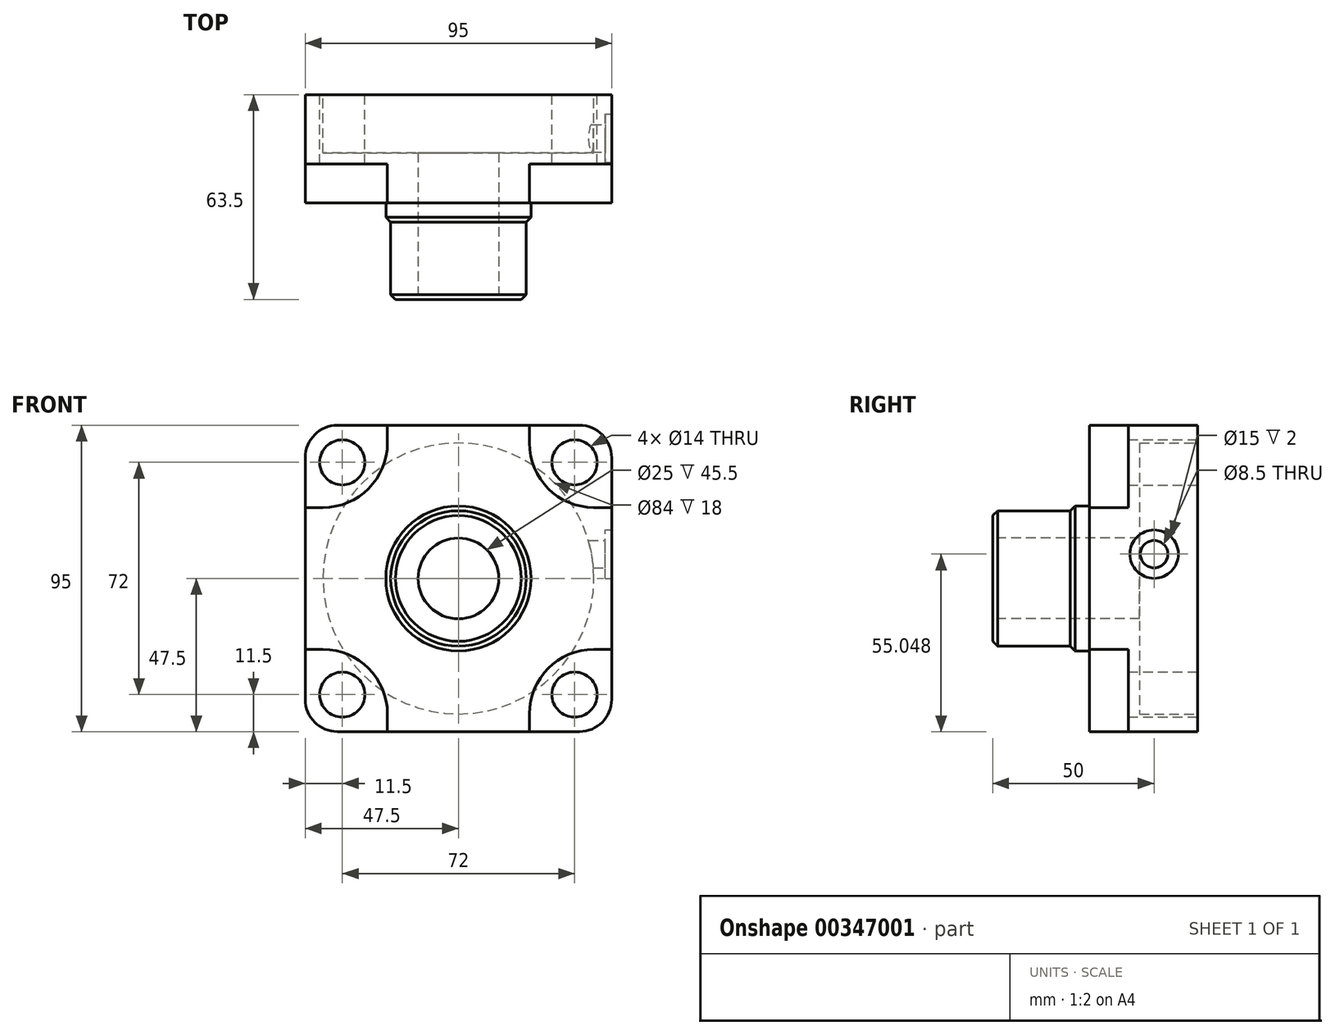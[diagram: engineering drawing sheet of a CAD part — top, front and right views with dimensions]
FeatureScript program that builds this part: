
annotation { "Feature Type Name" : "Feature", "Feature Type Description" : "" }
export const myFeature = defineFeature(function(context is Context, id is Id, definition is map)
    precondition{}
    {
        {
            var Q0;
            Q0=qCreatedBy(makeId("Front.planeOp"),FACE);
            var sketch = newSketch(context, id + "F0", { "sketchPlane" : qUnion([Q0])});
            skLineSegment(sketch, "E0.bottom", {"start": v(37.5, -47.5) * mm, "end": v(-37.5, -47.5) * mm});
            skLineSegment(sketch, "E0.top", {"start": v(37.5, 47.5) * mm, "end": v(-37.5, 47.5) * mm});
            skLineSegment(sketch, "E0.left", {"start": v(47.5, -37.5) * mm, "end": v(47.5, 37.5) * mm});
            skLineSegment(sketch, "E0.right", {"start": v(-47.5, -37.5) * mm, "end": v(-47.5, 37.5) * mm});
            skPoint(sketch, "E0.middle", {"position": v(0, 0) * mm});
            skPoint(sketch, "E1.visualSharp", {"position": v(-47.5, 47.5) * mm});
            skArc(sketch, "E1.filletArc", {"start": v(-37.5, 47.5) * mm, "mid": v(-44.57, 44.57) * mm, "end": v(-47.5, 37.5) * mm});
            skPoint(sketch, "E2.visualSharp", {"position": v(47.5, 47.5) * mm});
            skArc(sketch, "E2.filletArc", {"start": v(47.5, 37.5) * mm, "mid": v(44.57, 44.57) * mm, "end": v(37.5, 47.5) * mm});
            skPoint(sketch, "E3.visualSharp", {"position": v(47.5, -47.5) * mm});
            skArc(sketch, "E3.filletArc", {"start": v(37.5, -47.5) * mm, "mid": v(44.57, -44.57) * mm, "end": v(47.5, -37.5) * mm});
            skPoint(sketch, "E4.visualSharp", {"position": v(-47.5, -47.5) * mm});
            skArc(sketch, "E4.filletArc", {"start": v(-47.5, -37.5) * mm, "mid": v(-44.57, -44.57) * mm, "end": v(-37.5, -47.5) * mm});
            skLineSegment(sketch, "E5", {"start": v(0, 47.5) * mm, "end": v(0, -47.5) * mm, "construction": true});
            skLineSegment(sketch, "E6.0", {"start": v(-36, 47.5) * mm, "end": v(-36, -47.5) * mm, "construction": true});
            skLineSegment(sketch, "E7.0", {"start": v(36, 47.5) * mm, "end": v(36, -47.5) * mm, "construction": true});
            skLineSegment(sketch, "E8", {"start": v(-47.5, 0) * mm, "end": v(47.5, 0) * mm, "construction": true});
            skLineSegment(sketch, "E9.0", {"start": v(-47.5, -36) * mm, "end": v(47.5, -36) * mm, "construction": true});
            skLineSegment(sketch, "E10.0", {"start": v(-47.5, 36) * mm, "end": v(47.5, 36) * mm, "construction": true});
            skCircle(sketch, "E11", {"center": v(-36, 36) * mm, "radius": 7 * mm});
            skCircle(sketch, "E12", {"center": v(36, 36) * mm, "radius": 7 * mm});
            skCircle(sketch, "E13", {"center": v(-36, -36) * mm, "radius": 7 * mm});
            skCircle(sketch, "E14", {"center": v(36, -36) * mm, "radius": 7 * mm});
            skSolve(sketch);
        }
        {
            var Q0;
            Q0=makeQuery(id+"F0.imprint","IMPRINT",FACE,{"disambiguationData":[TD([[makeQuery(id+"F0.imprint","IMPRINT",EDGE,{"derivedFrom":sQuery(id+"F0.wireOp",EDGE,"E0.bottom")}),-1.0]])]});
            extrude(context, id + "F1", {"entities" : qUnion([Q0]), "endBound" : BoundingType.SYMMETRIC, "depth" : 33.5 * mm});
        }
        {
            var Q0;
            Q0=makeQuery(id+"F1.opExtrude","CAP_FACE",FACE,{"disambiguationData":[OSD([sQuery(id+"F0.wireOp",EDGE,"E0.bottom"),sQuery(id+"F0.wireOp",EDGE,"E0.top"),sQuery(id+"F0.wireOp",EDGE,"E0.left"),sQuery(id+"F0.wireOp",EDGE,"E0.right"),sQuery(id+"F0.wireOp",EDGE,"E1.filletArc"),sQuery(id+"F0.wireOp",EDGE,"E2.filletArc"),sQuery(id+"F0.wireOp",EDGE,"E3.filletArc"),sQuery(id+"F0.wireOp",EDGE,"E4.filletArc"),sQuery(id+"F0.wireOp",EDGE,"E11"),sQuery(id+"F0.wireOp",EDGE,"E12"),sQuery(id+"F0.wireOp",EDGE,"E13"),sQuery(id+"F0.wireOp",EDGE,"E14")])],"isStart":false});
            var sketch = newSketch(context, id + "F2", { "sketchPlane" : qUnion([Q0])});
            skLineSegment(sketch, "E15", {"start": v(-47.5, 22) * mm, "end": v(-42, 22) * mm});
            skLineSegment(sketch, "E16", {"start": v(-47.5, -22) * mm, "end": v(-42, -22) * mm});
            skLineSegment(sketch, "E17", {"start": v(-22, 47.5) * mm, "end": v(-22, 42) * mm});
            skLineSegment(sketch, "E18", {"start": v(22, 47.5) * mm, "end": v(22, 42) * mm});
            skLineSegment(sketch, "E19", {"start": v(42, 22) * mm, "end": v(47.5, 22) * mm});
            skLineSegment(sketch, "E20", {"start": v(42, -22) * mm, "end": v(47.5, -22) * mm});
            skLineSegment(sketch, "E21", {"start": v(22, -42) * mm, "end": v(22, -47.5) * mm});
            skLineSegment(sketch, "E22", {"start": v(-22, -42) * mm, "end": v(-22, -47.5) * mm});
            skArc(sketch, "E23.filletArc", {"start": v(-42, 22) * mm, "mid": v(-27.86, 27.86) * mm, "end": v(-22, 42) * mm});
            skPoint(sketch, "E24.newPointA", {"position": v(0.48, 22) * mm});
            skArc(sketch, "E24.filletArc", {"start": v(22, 42) * mm, "mid": v(27.86, 27.86) * mm, "end": v(42, 22) * mm});
            skPoint(sketch, "E25.newPointB", {"position": v(-22, -0.08) * mm});
            skArc(sketch, "E25.filletArc", {"start": v(-22, -42) * mm, "mid": v(-27.86, -27.86) * mm, "end": v(-42, -22) * mm});
            skPoint(sketch, "E26.newPointA", {"position": v(1.13, -22) * mm});
            skPoint(sketch, "E26.newPointB", {"position": v(22, -0.08) * mm});
            skArc(sketch, "E26.filletArc", {"start": v(42, -22) * mm, "mid": v(27.86, -27.86) * mm, "end": v(22, -42) * mm});
            skLineSegment(sketch, "E27.0", {"start": v(-47.5, -37.5) * mm, "end": v(-47.5, -22) * mm});
            skArc(sketch, "E28.0", {"start": v(-37.5, 47.5) * mm, "mid": v(-44.57, 44.57) * mm, "end": v(-47.5, 37.5) * mm});
            skLineSegment(sketch, "E29.0", {"start": v(37.5, 47.5) * mm, "end": v(22, 47.5) * mm});
            skPoint(sketch, "E30.0", {"position": v(44.57, 44.57) * mm});
            skArc(sketch, "E31.0", {"start": v(47.5, 37.5) * mm, "mid": v(44.57, 44.57) * mm, "end": v(37.5, 47.5) * mm});
            skLineSegment(sketch, "E32.0", {"start": v(47.5, -37.5) * mm, "end": v(47.5, -22) * mm});
            skPoint(sketch, "E33.0", {"position": v(44.57, -44.57) * mm});
            skArc(sketch, "E34.0", {"start": v(37.5, -47.5) * mm, "mid": v(44.57, -44.57) * mm, "end": v(47.5, -37.5) * mm});
            skLineSegment(sketch, "E35.0", {"start": v(37.5, -47.5) * mm, "end": v(22, -47.5) * mm});
            skArc(sketch, "E36.0", {"start": v(-47.5, -37.5) * mm, "mid": v(-44.57, -44.57) * mm, "end": v(-37.5, -47.5) * mm});
            skPoint(sketch, "E37.orphan", {"position": v(-51.1, 22) * mm});
            skPoint(sketch, "E38.orphan", {"position": v(-22, 52.95) * mm});
            skLineSegment(sketch, "E39.trimOffspring", {"start": v(-22, 47.5) * mm, "end": v(-37.5, 47.5) * mm});
            skLineSegment(sketch, "E40.trimOffspring", {"start": v(-47.5, 22) * mm, "end": v(-47.5, 37.5) * mm});
            skPoint(sketch, "E41.orphan", {"position": v(-22, -53.12) * mm});
            skPoint(sketch, "E42.orphan", {"position": v(-51.1, -22) * mm});
            skLineSegment(sketch, "E43.trimOffspring", {"start": v(-22, -47.5) * mm, "end": v(-37.5, -47.5) * mm});
            skPoint(sketch, "E44.orphan", {"position": v(22, -51.66) * mm});
            skPoint(sketch, "E45.orphan", {"position": v(53.36, -22) * mm});
            skPoint(sketch, "E46.orphan", {"position": v(52.07, 22) * mm});
            skPoint(sketch, "E47.orphan", {"position": v(22, 51.5) * mm});
            skLineSegment(sketch, "E48.trimOffspring", {"start": v(47.5, 22) * mm, "end": v(47.5, 37.5) * mm});
            skSolve(sketch);
        }
        {
            var Q0;
            Q0=makeQuery(id+"F2.imprint","IMPRINT",FACE,{"disambiguationData":[TD([[makeQuery(id+"F2.imprint","IMPRINT",EDGE,{"derivedFrom":sQuery(id+"F2.wireOp",EDGE,"E20")}),-1.0]])]});
            var Q1;
            Q1=makeQuery(id+"F2.imprint","IMPRINT",FACE,{"disambiguationData":[TD([[makeQuery(id+"F2.imprint","IMPRINT",EDGE,{"derivedFrom":sQuery(id+"F2.wireOp",EDGE,"E18")}),1.0]])]});
            var Q2;
            Q2=makeQuery(id+"F2.imprint","IMPRINT",FACE,{"disambiguationData":[TD([[makeQuery(id+"F2.imprint","IMPRINT",EDGE,{"derivedFrom":sQuery(id+"F2.wireOp",EDGE,"E15")}),1.0]])]});
            var Q3;
            Q3=makeQuery(id+"F2.imprint","IMPRINT",FACE,{"disambiguationData":[TD([[makeQuery(id+"F2.imprint","IMPRINT",EDGE,{"derivedFrom":sQuery(id+"F2.wireOp",EDGE,"E16")}),-1.0]])]});
            extrude(context, id + "F3", {"entities" : qUnion([Q0, Q1, Q2, Q3]), "operationType" : NewBodyOperationType.REMOVE, "oppositeDirection" : true, "depth" : 12 * mm});
        }
        {
            var Q0;
            Q0=makeQuery(id+"F1.opExtrude","CAP_FACE",FACE,{"disambiguationData":[OSD([sQuery(id+"F0.wireOp",EDGE,"E0.bottom"),sQuery(id+"F0.wireOp",EDGE,"E0.top"),sQuery(id+"F0.wireOp",EDGE,"E0.left"),sQuery(id+"F0.wireOp",EDGE,"E0.right"),sQuery(id+"F0.wireOp",EDGE,"E1.filletArc"),sQuery(id+"F0.wireOp",EDGE,"E2.filletArc"),sQuery(id+"F0.wireOp",EDGE,"E3.filletArc"),sQuery(id+"F0.wireOp",EDGE,"E4.filletArc"),sQuery(id+"F0.wireOp",EDGE,"E11"),sQuery(id+"F0.wireOp",EDGE,"E12"),sQuery(id+"F0.wireOp",EDGE,"E13"),sQuery(id+"F0.wireOp",EDGE,"E14")])],"isStart":false});
            var sketch = newSketch(context, id + "F4", { "sketchPlane" : qUnion([Q0])});
            skCircle(sketch, "E49", {"center": v(0, 0) * mm, "radius": 22.5 * mm});
            skSolve(sketch);
        }
        {
            var Q0;
            Q0=makeQuery(id+"F4.imprint","IMPRINT",FACE,{"disambiguationData":[TD([[makeQuery(id+"F4.imprint","IMPRINT",EDGE,{"derivedFrom":sQuery(id+"F4.wireOp",EDGE,"E49")}),1.0]])]});
            extrude(context, id + "F5", {"entities" : qUnion([Q0]), "operationType" : NewBodyOperationType.ADD, "depth" : 6 * mm});
        }
        {
            var Q0;
            Q0=makeQuery(id+"F5.opExtrude","CAP_EDGE",EDGE,{"disambiguationData":[OSD([sQuery(id+"F4.wireOp",EDGE,"E49")])],"isStart":false});
            chamfer(context, id + "F6", {"entities" : qUnion([Q0]), "width" : 1.5 * mm, "tangentPropagation" : true});
        }
        {
            var Q0;
            Q0=makeQuery(id+"F5.opExtrude","CAP_FACE",FACE,{"disambiguationData":[OSD([sQuery(id+"F4.wireOp",EDGE,"E49")])],"isStart":false});
            var sketch = newSketch(context, id + "F7", { "sketchPlane" : qUnion([Q0])});
            skCircle(sketch, "E50.0", {"center": v(0, 0) * mm, "radius": 21 * mm});
            skSolve(sketch);
        }
        {
            var Q0;
            Q0=makeQuery(id+"F7.imprint","IMPRINT",FACE,{"disambiguationData":[TD([[makeQuery(id+"F7.imprint","IMPRINT",EDGE,{"derivedFrom":sQuery(id+"F7.wireOp",EDGE,"E50.0")}),1.0]])]});
            extrude(context, id + "F8", {"entities" : qUnion([Q0]), "operationType" : NewBodyOperationType.ADD, "depth" : 24 * mm});
        }
        {
            var Q0;
            Q0=makeQuery(id+"F8.opExtrude","CAP_EDGE",EDGE,{"disambiguationData":[OSD([sQuery(id+"F7.wireOp",EDGE,"E50.0")])],"isStart":false});
            chamfer(context, id + "F9", {"entities" : qUnion([Q0]), "width" : 1.5 * mm, "tangentPropagation" : true});
        }
        {
            var Q0;
            Q0=makeQuery(id+"F8.opExtrude","CAP_FACE",FACE,{"disambiguationData":[OSD([sQuery(id+"F7.wireOp",EDGE,"E50.0")])],"isStart":false});
            var sketch = newSketch(context, id + "F10", { "sketchPlane" : qUnion([Q0])});
            skCircle(sketch, "E51", {"center": v(0, 0) * mm, "radius": 12.5 * mm});
            skSolve(sketch);
        }
        {
            var Q0;
            Q0=makeQuery(id+"F10.imprint","IMPRINT",FACE,{"disambiguationData":[TD([[makeQuery(id+"F10.imprint","IMPRINT",EDGE,{"derivedFrom":sQuery(id+"F10.wireOp",EDGE,"E51")}),1.0]])]});
            extrude(context, id + "F11", {"entities" : qUnion([Q0]), "operationType" : NewBodyOperationType.REMOVE, "endBound" : BoundingType.THROUGH_ALL, "oppositeDirection" : true, "depth" : 25 * mm});
        }
        {
            var Q0;
            Q0=makeQuery(id+"F1.opExtrude","CAP_FACE",FACE,{"disambiguationData":[OSD([sQuery(id+"F0.wireOp",EDGE,"E0.bottom"),sQuery(id+"F0.wireOp",EDGE,"E0.top"),sQuery(id+"F0.wireOp",EDGE,"E0.left"),sQuery(id+"F0.wireOp",EDGE,"E0.right"),sQuery(id+"F0.wireOp",EDGE,"E1.filletArc"),sQuery(id+"F0.wireOp",EDGE,"E2.filletArc"),sQuery(id+"F0.wireOp",EDGE,"E3.filletArc"),sQuery(id+"F0.wireOp",EDGE,"E4.filletArc"),sQuery(id+"F0.wireOp",EDGE,"E11"),sQuery(id+"F0.wireOp",EDGE,"E12"),sQuery(id+"F0.wireOp",EDGE,"E13"),sQuery(id+"F0.wireOp",EDGE,"E14")])],"isStart":true});
            var sketch = newSketch(context, id + "F12", { "sketchPlane" : qUnion([Q0])});
            skCircle(sketch, "E52", {"center": v(0, 0) * mm, "radius": 42 * mm});
            skSolve(sketch);
        }
        {
            var Q0;
            Q0=makeQuery(id+"F12.imprint","IMPRINT",FACE,{"disambiguationData":[TD([[makeQuery(id+"F12.imprint","IMPRINT",EDGE,{"derivedFrom":sQuery(id+"F12.wireOp",EDGE,"E52")}),1.0]])]});
            extrude(context, id + "F13", {"entities" : qUnion([Q0]), "operationType" : NewBodyOperationType.REMOVE, "oppositeDirection" : true, "depth" : 18 * mm});
        }
        {
            var Q0;
            Q0=makeQuery(id+"F1.opExtrude","SWEPT_FACE",FACE,{"disambiguationData":[OSD([sQuery(id+"F0.wireOp",EDGE,"E0.left")])]});
            var sketch = newSketch(context, id + "F14", { "sketchPlane" : qUnion([Q0])});
            skLineSegment(sketch, "E53", {"start": v(3.25, 48.9) * mm, "end": v(3.25, -49.62) * mm, "construction": true});
            skCircle(sketch, "E54", {"center": v(3.25, 7.55) * mm, "radius": 4.25 * mm});
            skCircle(sketch, "E55", {"center": v(3.25, 7.55) * mm, "radius": 7.5 * mm});
            skSolve(sketch);
        }
        {
            var Q0;
            Q0=makeQuery(id+"F14.imprint","IMPRINT",FACE,{"disambiguationData":[TD([[makeQuery(id+"F14.imprint","IMPRINT",EDGE,{"derivedFrom":sQuery(id+"F14.wireOp",EDGE,"E54")}),-1.0]])]});
            extrude(context, id + "F15", {"entities" : qUnion([Q0]), "operationType" : NewBodyOperationType.REMOVE, "oppositeDirection" : true, "depth" : 2 * mm});
        }
        {
            var Q0;
            Q0=makeQuery(id+"F15.boolean.opBoolean","SPLIT",FACE,{"disambiguationData":[TD([makeQuery(id+"F15.opExtrude","SWEPT_FACE",FACE,{"disambiguationData":[OSD([sQuery(id+"F14.wireOp",EDGE,"E54")])]})])],"derivedFrom":makeQuery(id+"F1.opExtrude","SWEPT_FACE",FACE,{"disambiguationData":[OSD([sQuery(id+"F0.wireOp",EDGE,"E0.left")])]})});
            extrude(context, id + "F16", {"entities" : qUnion([Q0]), "operationType" : NewBodyOperationType.REMOVE, "oppositeDirection" : true, "depth" : 9 * mm});
        }
    });
